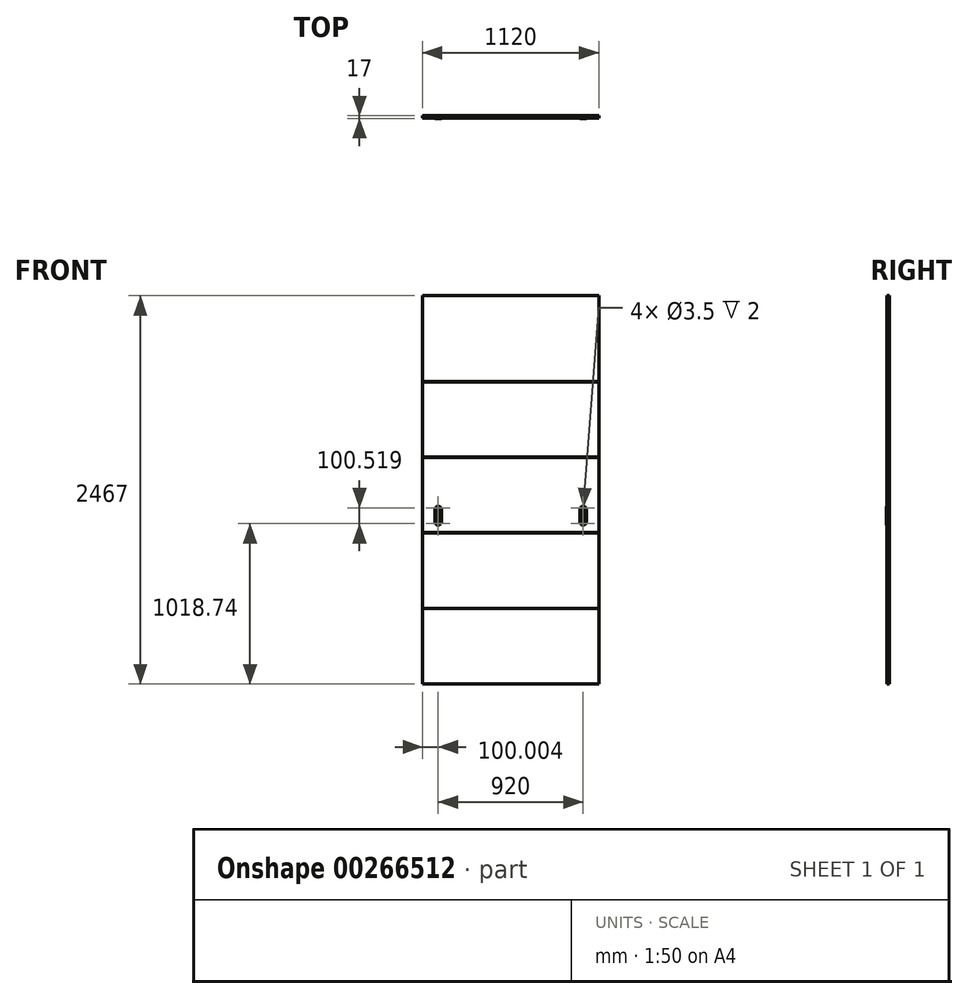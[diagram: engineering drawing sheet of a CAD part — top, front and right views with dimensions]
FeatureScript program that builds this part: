
annotation { "Feature Type Name" : "Feature", "Feature Type Description" : "" }
export const myFeature = defineFeature(function(context is Context, id is Id, definition is map)
    precondition{}
    {
        {
            var Q0;
            Q0=qCreatedBy(makeId("Front.planeOp"),FACE);
            var sketch = newSketch(context, id + "F0", { "sketchPlane" : qUnion([Q0])});
            skLineSegment(sketch, "E0.bottom", {"start": v(-661.76, 1229.1) * mm, "end": v(458.24, 1229.1) * mm});
            skLineSegment(sketch, "E0.top", {"start": v(-661.76, -1237.9) * mm, "end": v(458.24, -1237.9) * mm});
            skLineSegment(sketch, "E0.left", {"start": v(-661.76, 1229.1) * mm, "end": v(-661.76, -1237.9) * mm});
            skLineSegment(sketch, "E0.right", {"start": v(458.24, 1229.1) * mm, "end": v(458.24, -1237.9) * mm});
            skSolve(sketch);
        }
        {
            var Q0;
            Q0=makeQuery(id+"F0.imprint","IMPRINT",FACE,{"disambiguationData":[TD([[makeQuery(id+"F0.imprint","IMPRINT",EDGE,{"derivedFrom":sQuery(id+"F0.wireOp",EDGE,"E0.bottom")}),-1.0]])]});
            extrude(context, id + "F1", {"entities" : qUnion([Q0]), "depth" : 15 * mm});
        }
        {
            var Q0;
            Q0=makeQuery(id+"F1.opExtrude","SWEPT_FACE",FACE,{"disambiguationData":[OSD([sQuery(id+"F0.wireOp",EDGE,"E0.left")])]});
            var sketch = newSketch(context, id + "F2", { "sketchPlane" : qUnion([Q0])});
            skLineSegment(sketch, "E1", {"start": v(-467.06, -757.9) * mm, "end": v(625.08, -757.9) * mm, "construction": true});
            skLineSegment(sketch, "E2", {"start": v(625.08, -277.9) * mm, "end": v(-589.97, -277.9) * mm, "construction": true});
            skLineSegment(sketch, "E3", {"start": v(-589.97, 202.1) * mm, "end": v(575.92, 202.1) * mm, "construction": true});
            skLineSegment(sketch, "E4", {"start": v(575.92, 682.1) * mm, "end": v(-586.45, 682.1) * mm, "construction": true});
            skLineSegment(sketch, "E5", {"start": v(-586.45, 1229.1) * mm, "end": v(554.85, 1229.1) * mm, "construction": true});
            skLineSegment(sketch, "E6", {"start": v(0, -1237.9) * mm, "end": v(-639.13, -1237.9) * mm, "construction": true});
            skLineSegment(sketch, "E7", {"start": v(15, -756.9) * mm, "end": v(14, -757.9) * mm});
            skLineSegment(sketch, "E8", {"start": v(15, -756.9) * mm, "end": v(15, -757.9) * mm});
            skLineSegment(sketch, "E9.MirrorCS", {"start": v(15, -758.9) * mm, "end": v(14, -757.9) * mm});
            skLineSegment(sketch, "E10.MirrorCS", {"start": v(15, -758.9) * mm, "end": v(15, -757.9) * mm});
            skLineSegment(sketch, "E11", {"start": v(384.77, -277.9) * mm, "end": v(384.77, -757.9) * mm, "construction": true});
            skLineSegment(sketch, "E12", {"start": v(384.77, -517.9) * mm, "end": v(-286.08, -517.9) * mm, "construction": true});
            skLineSegment(sketch, "E13.MirrorCS", {"start": v(15, 683.1) * mm, "end": v(15, 682.1) * mm});
            skLineSegment(sketch, "E14.MirrorCS", {"start": v(15, 683.1) * mm, "end": v(14, 682.1) * mm});
            skLineSegment(sketch, "E15.MirrorCS", {"start": v(15, 681.1) * mm, "end": v(14, 682.1) * mm});
            skLineSegment(sketch, "E16.MirrorCS", {"start": v(15, 681.1) * mm, "end": v(15, 682.1) * mm});
            skLineSegment(sketch, "E17.MirrorCS", {"start": v(15, -278.9) * mm, "end": v(15, -277.9) * mm});
            skLineSegment(sketch, "E18.MirrorCS", {"start": v(15, -276.9) * mm, "end": v(14, -277.9) * mm});
            skLineSegment(sketch, "E19.MirrorCS", {"start": v(15, -278.9) * mm, "end": v(14, -277.9) * mm});
            skLineSegment(sketch, "E20.MirrorCS", {"start": v(15, -276.9) * mm, "end": v(15, -277.9) * mm});
            skLineSegment(sketch, "E21.MirrorCS", {"start": v(15, 201.1) * mm, "end": v(15, 202.1) * mm});
            skLineSegment(sketch, "E22.MirrorCS", {"start": v(15, 203.1) * mm, "end": v(14, 202.1) * mm});
            skLineSegment(sketch, "E23.MirrorCS", {"start": v(15, 201.1) * mm, "end": v(14, 202.1) * mm});
            skLineSegment(sketch, "E24.MirrorCS", {"start": v(15, 203.1) * mm, "end": v(15, 202.1) * mm});
            skSolve(sketch);
        }
        {
            var Q0;
            Q0=qSketchRegion(id+"F2",true);
            extrude(context, id + "F3", {"entities" : qUnion([Q0]), "operationType" : NewBodyOperationType.REMOVE, "endBound" : BoundingType.THROUGH_ALL, "oppositeDirection" : true, "depth" : 25 * mm});
        }
        {
            var Q0;
            {var subQ0=sQuery(id+"F0.wireOp",EDGE,"E0.left");var subQ1=sQuery(id+"F0.wireOp",EDGE,"E0.right");Q0=makeQuery(id+"F3.boolean.opBoolean","SPLIT",FACE,{"disambiguationData":[TD([makeQuery(id+"F3.opExtrude","SWEPT_FACE",FACE,{"disambiguationData":[OSD([sQuery(id+"F2.wireOp",EDGE,"E18.MirrorCS")])]})])],"derivedFrom":makeQuery(id+"F1.opExtrude","CAP_FACE",FACE,{"disambiguationData":[OSD([sQuery(id+"F0.wireOp",EDGE,"E0.bottom"),sQuery(id+"F0.wireOp",EDGE,"E0.top"),subQ0,subQ1])],"isStart":false})});}
            var sketch = newSketch(context, id + "F4", { "sketchPlane" : qUnion([Q0])});
            skArc(sketch, "E25", {"start": v(372.24, -137.9) * mm, "mid": v(358.24, -123.9) * mm, "end": v(344.24, -137.9) * mm});
            skLineSegment(sketch, "E26", {"start": v(358.24, -137.9) * mm, "end": v(-308.77, -137.9) * mm, "construction": true});
            skLineSegment(sketch, "E27", {"start": v(344.24, -137.9) * mm, "end": v(344.24, -199.9) * mm});
            skArc(sketch, "E28", {"start": v(344.24, -199.9) * mm, "mid": v(358.24, -213.9) * mm, "end": v(372.24, -199.9) * mm});
            skLineSegment(sketch, "E29", {"start": v(372.24, -137.9) * mm, "end": v(372.24, -199.9) * mm});
            skArc(sketch, "E30", {"start": v(370.24, -137.9) * mm, "mid": v(358.24, -125.9) * mm, "end": v(346.24, -137.9) * mm});
            skArc(sketch, "E31", {"start": v(346.24, -199.9) * mm, "mid": v(358.24, -211.9) * mm, "end": v(370.24, -199.9) * mm});
            skLineSegment(sketch, "E32", {"start": v(346.24, -137.9) * mm, "end": v(346.24, -199.9) * mm});
            skLineSegment(sketch, "E33", {"start": v(370.24, -137.9) * mm, "end": v(370.24, -199.9) * mm});
            skLineSegment(sketch, "E34", {"start": v(358.24, -105.6) * mm, "end": v(358.24, -199.9) * mm, "construction": true});
            skLineSegment(sketch, "E35", {"start": v(394.55, -168.9) * mm, "end": v(321.36, -168.9) * mm, "construction": true});
            skPoint(sketch, "E36.orphan", {"position": v(358.24, -168.9) * mm});
            skLineSegment(sketch, "E37", {"start": v(338.24, -168.9) * mm, "end": v(338.24, -128.9) * mm});
            skArc(sketch, "E38.trimOffspring", {"start": v(358.24, -108.9) * mm, "mid": v(344.1, -114.75) * mm, "end": v(338.24, -128.9) * mm});
            skArc(sketch, "E39.MirrorCS", {"start": v(358.24, -108.9) * mm, "mid": v(372.39, -114.75) * mm, "end": v(378.24, -128.9) * mm});
            skLineSegment(sketch, "E40.MirrorCS", {"start": v(378.24, -168.9) * mm, "end": v(378.24, -128.9) * mm});
            skLineSegment(sketch, "E41.MirrorCS", {"start": v(338.24, -168.9) * mm, "end": v(338.24, -208.9) * mm});
            skArc(sketch, "E42.MirrorCS", {"start": v(358.24, -228.9) * mm, "mid": v(344.1, -223.03) * mm, "end": v(338.24, -208.9) * mm});
            skArc(sketch, "E43.MirrorCS", {"start": v(358.24, -228.9) * mm, "mid": v(372.39, -223.03) * mm, "end": v(378.24, -208.9) * mm});
            skLineSegment(sketch, "E44.MirrorCS", {"start": v(378.24, -168.9) * mm, "end": v(378.24, -208.9) * mm});
            skCircle(sketch, "E45", {"center": v(358.24, -118.63) * mm, "radius": 1.75 * mm});
            skCircle(sketch, "E46.MirrorC", {"center": v(358.24, -219.15) * mm, "radius": 1.75 * mm});
            skArc(sketch, "E47", {"start": v(-547.76, -137.9) * mm, "mid": v(-561.76, -123.9) * mm, "end": v(-575.76, -137.9) * mm});
            skLineSegment(sketch, "E48", {"start": v(-41, -137.9) * mm, "end": v(-561.76, -137.9) * mm, "construction": true});
            skLineSegment(sketch, "E49", {"start": v(-575.76, -137.9) * mm, "end": v(-575.76, -199.9) * mm});
            skArc(sketch, "E50", {"start": v(-575.76, -199.9) * mm, "mid": v(-561.76, -213.9) * mm, "end": v(-547.76, -199.9) * mm});
            skLineSegment(sketch, "E51", {"start": v(-547.76, -137.9) * mm, "end": v(-547.76, -199.9) * mm});
            skArc(sketch, "E52", {"start": v(-549.76, -137.9) * mm, "mid": v(-561.76, -125.9) * mm, "end": v(-573.76, -137.9) * mm});
            skArc(sketch, "E53", {"start": v(-573.76, -199.9) * mm, "mid": v(-561.76, -211.9) * mm, "end": v(-549.76, -199.9) * mm});
            skLineSegment(sketch, "E54", {"start": v(-573.76, -137.9) * mm, "end": v(-573.76, -199.9) * mm});
            skLineSegment(sketch, "E55", {"start": v(-549.76, -137.9) * mm, "end": v(-549.76, -199.9) * mm});
            skLineSegment(sketch, "E56", {"start": v(-561.76, -105.6) * mm, "end": v(-561.76, -199.9) * mm, "construction": true});
            skLineSegment(sketch, "E57", {"start": v(37.23, -168.9) * mm, "end": v(-35.96, -168.9) * mm, "construction": true});
            skPoint(sketch, "E58.orphan", {"position": v(-561.76, -168.9) * mm});
            skLineSegment(sketch, "E59", {"start": v(-581.76, -168.9) * mm, "end": v(-581.76, -128.9) * mm});
            skArc(sketch, "E60.trimOffspring", {"start": v(-561.76, -108.9) * mm, "mid": v(-575.9, -114.75) * mm, "end": v(-581.76, -128.9) * mm});
            skArc(sketch, "E61.MirrorCS", {"start": v(-561.76, -108.9) * mm, "mid": v(-547.61, -114.75) * mm, "end": v(-541.76, -128.9) * mm});
            skLineSegment(sketch, "E62.MirrorCS", {"start": v(-541.76, -168.9) * mm, "end": v(-541.76, -128.9) * mm});
            skLineSegment(sketch, "E63.MirrorCS", {"start": v(-581.76, -168.9) * mm, "end": v(-581.76, -208.9) * mm});
            skArc(sketch, "E64.MirrorCS", {"start": v(-561.76, -228.9) * mm, "mid": v(-575.9, -223.03) * mm, "end": v(-581.76, -208.9) * mm});
            skArc(sketch, "E65.MirrorCS", {"start": v(-561.76, -228.9) * mm, "mid": v(-547.61, -223.03) * mm, "end": v(-541.76, -208.9) * mm});
            skLineSegment(sketch, "E66.MirrorCS", {"start": v(-541.76, -168.9) * mm, "end": v(-541.76, -208.9) * mm});
            skCircle(sketch, "E67", {"center": v(-561.76, -118.63) * mm, "radius": 1.75 * mm});
            skCircle(sketch, "E68.MirrorC", {"center": v(-561.76, -219.15) * mm, "radius": 1.75 * mm});
            skSolve(sketch);
        }
        {
            var Q0;
            Q0=makeQuery(id+"F4.imprint","IMPRINT",FACE,{"disambiguationData":[TD([[makeQuery(id+"F4.imprint","IMPRINT",EDGE,{"derivedFrom":sQuery(id+"F4.wireOp",EDGE,"E30")}),1.0]])]});
            var Q1;
            Q1=makeQuery(id+"F4.imprint","IMPRINT",FACE,{"disambiguationData":[TD([[makeQuery(id+"F4.imprint","IMPRINT",EDGE,{"derivedFrom":sQuery(id+"F4.wireOp",EDGE,"E25")}),1.0]])]});
            var Q2;
            Q2=makeQuery(id+"F4.imprint","IMPRINT",FACE,{"disambiguationData":[TD([[makeQuery(id+"F4.imprint","IMPRINT",EDGE,{"derivedFrom":sQuery(id+"F4.wireOp",EDGE,"E52")}),1.0]])]});
            var Q3;
            Q3=makeQuery(id+"F4.imprint","IMPRINT",FACE,{"disambiguationData":[TD([[makeQuery(id+"F4.imprint","IMPRINT",EDGE,{"derivedFrom":sQuery(id+"F4.wireOp",EDGE,"E47")}),1.0]])]});
            extrude(context, id + "F5", {"entities" : qUnion([Q0, Q1, Q2, Q3]), "operationType" : NewBodyOperationType.REMOVE, "oppositeDirection" : true, "depth" : 13 * mm});
        }
        {
            var Q0;
            Q0=makeQuery(id+"F4.imprint","IMPRINT",FACE,{"disambiguationData":[TD([[makeQuery(id+"F4.imprint","IMPRINT",EDGE,{"derivedFrom":sQuery(id+"F4.wireOp",EDGE,"E25")}),1.0]])]});
            var Q1;
            Q1=makeQuery(id+"F4.imprint","IMPRINT",FACE,{"disambiguationData":[TD([[makeQuery(id+"F4.imprint","IMPRINT",EDGE,{"derivedFrom":sQuery(id+"F4.wireOp",EDGE,"E47")}),1.0]])]});
            extrude(context, id + "F6", {"entities" : qUnion([Q0, Q1]), "oppositeDirection" : true, "depth" : 13 * mm});
        }
        {
            var Q0;
            Q0=makeQuery(id+"F4.imprint","IMPRINT",FACE,{"disambiguationData":[TD([[makeQuery(id+"F4.imprint","IMPRINT",EDGE,{"derivedFrom":sQuery(id+"F4.wireOp",EDGE,"E30")}),1.0]])]});
            extrude(context, id + "F7", {"entities" : qUnion([Q0]), "operationType" : NewBodyOperationType.ADD, "oppositeDirection" : true, "depth" : 13 * mm, "hasSecondDirection" : true, "secondDirectionOppositeDirection" : true, "secondDirectionDepth" : 11 * mm});
        }
        {
            var Q0;
            Q0=makeQuery(id+"F4.imprint","IMPRINT",FACE,{"disambiguationData":[TD([[makeQuery(id+"F4.imprint","IMPRINT",EDGE,{"derivedFrom":sQuery(id+"F4.wireOp",EDGE,"E25")}),-1.0]])]});
            var Q1;
            Q1=makeQuery(id+"F4.imprint","IMPRINT",FACE,{"disambiguationData":[TD([[makeQuery(id+"F4.imprint","IMPRINT",EDGE,{"derivedFrom":sQuery(id+"F4.wireOp",EDGE,"E25")}),1.0]])]});
            extrude(context, id + "F8", {"entities" : qUnion([Q0, Q1]), "operationType" : NewBodyOperationType.ADD, "depth" : 2 * mm});
        }
        {
            var Q0;
            Q0=makeQuery(id+"F5.boolean.opBoolean","COPY",FACE,{"derivedFrom":makeQuery(id+"F5.opExtrude","CAP_FACE",FACE,{"disambiguationData":[OSD([sQuery(id+"F4.wireOp",EDGE,"E47"),sQuery(id+"F4.wireOp",EDGE,"E49"),sQuery(id+"F4.wireOp",EDGE,"E50"),sQuery(id+"F4.wireOp",EDGE,"E51")])],"isStart":false})});
            extrude(context, id + "F9", {"entities" : qUnion([Q0]), "operationType" : NewBodyOperationType.ADD, "depth" : 2 * mm});
        }
        {
            var Q0;
            Q0=makeQuery(id+"F4.imprint","IMPRINT",FACE,{"disambiguationData":[TD([[makeQuery(id+"F4.imprint","IMPRINT",EDGE,{"derivedFrom":sQuery(id+"F4.wireOp",EDGE,"E47")}),-1.0]])]});
            var Q1;
            Q1=makeQuery(id+"F4.imprint","IMPRINT",FACE,{"disambiguationData":[TD([[makeQuery(id+"F4.imprint","IMPRINT",EDGE,{"derivedFrom":sQuery(id+"F4.wireOp",EDGE,"E47")}),1.0]])]});
            extrude(context, id + "F10", {"entities" : qUnion([Q0, Q1]), "operationType" : NewBodyOperationType.ADD, "depth" : 2 * mm});
        }
    });
